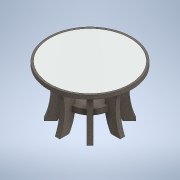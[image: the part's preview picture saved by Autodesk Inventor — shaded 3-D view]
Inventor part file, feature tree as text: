
AUTODESK INVENTOR PART (.ipt)
format: ipt  version: 2022 (Build 260153000, 153)  size: 234,496 bytes
history: native  units: mm
features: extrude x4, sketch x4, direct_edit x2, other x2, shell x1, pattern_circular x1, plane x1
ambient origin geometry x8: Origin, YZ Plane, XZ Plane, XY Plane, X Axis, Y Axis, Z Axis, Center Point
bodies: Solid1 (feature_tree), Solid2 (feature_tree), Solid3 (feature_tree), Solid4 (feature_tree)
feature tree (15):
  extrude  "Extrusion1"  Depth=2.0mm TaperAngle=0.0deg
  shell  "Shell1"  Thickness=1.0mm
  extrude  "Extrusion2"  Depth=1.0mm TaperAngle=0.0deg
  extrude  "Extrusion3"  Depth=25.0mm
  pattern_circular  "Circular Pattern1"  [2 undecoded]
  plane  "Work Plane1"
  extrude  "Extrusion4"  Depth=10.0mm
  direct_edit  "Direct Edit1"
  direct_edit  "Direct Edit2"
  sketch  "Sketch1"  dims[d0=45.0mm d1=2.0mm d2=0.0mm d3=1.0mm]
  sketch  "Sketch2"  dims[d4=43.0mm d5=1.0mm d6=0.0mm]
  sketch  "Sketch3"  dims[d7=5.0mm d8=25.0mm]
  sketch  "Sketch4"  dims[d9=25.0mm d10=5.0mm d11=5.0mm d12=2.5mm d13=0.0mm d14=80.0mm d15=360.0deg d17=12.5mm d18=20.0mm d19=2.5mm d20=0.0mm d21=7.5mm d22=10.0mm d23=10.0mm d24=9.0mm d25=10.0mm d26=10.0mm]
  other  "Scale1"
  other  "Scale2"
note: 2 required parameter values undecoded (feature->parameter linkage not recoverable at this tier; creation-order binding heuristic only, values carry confidence <= 0.55)
